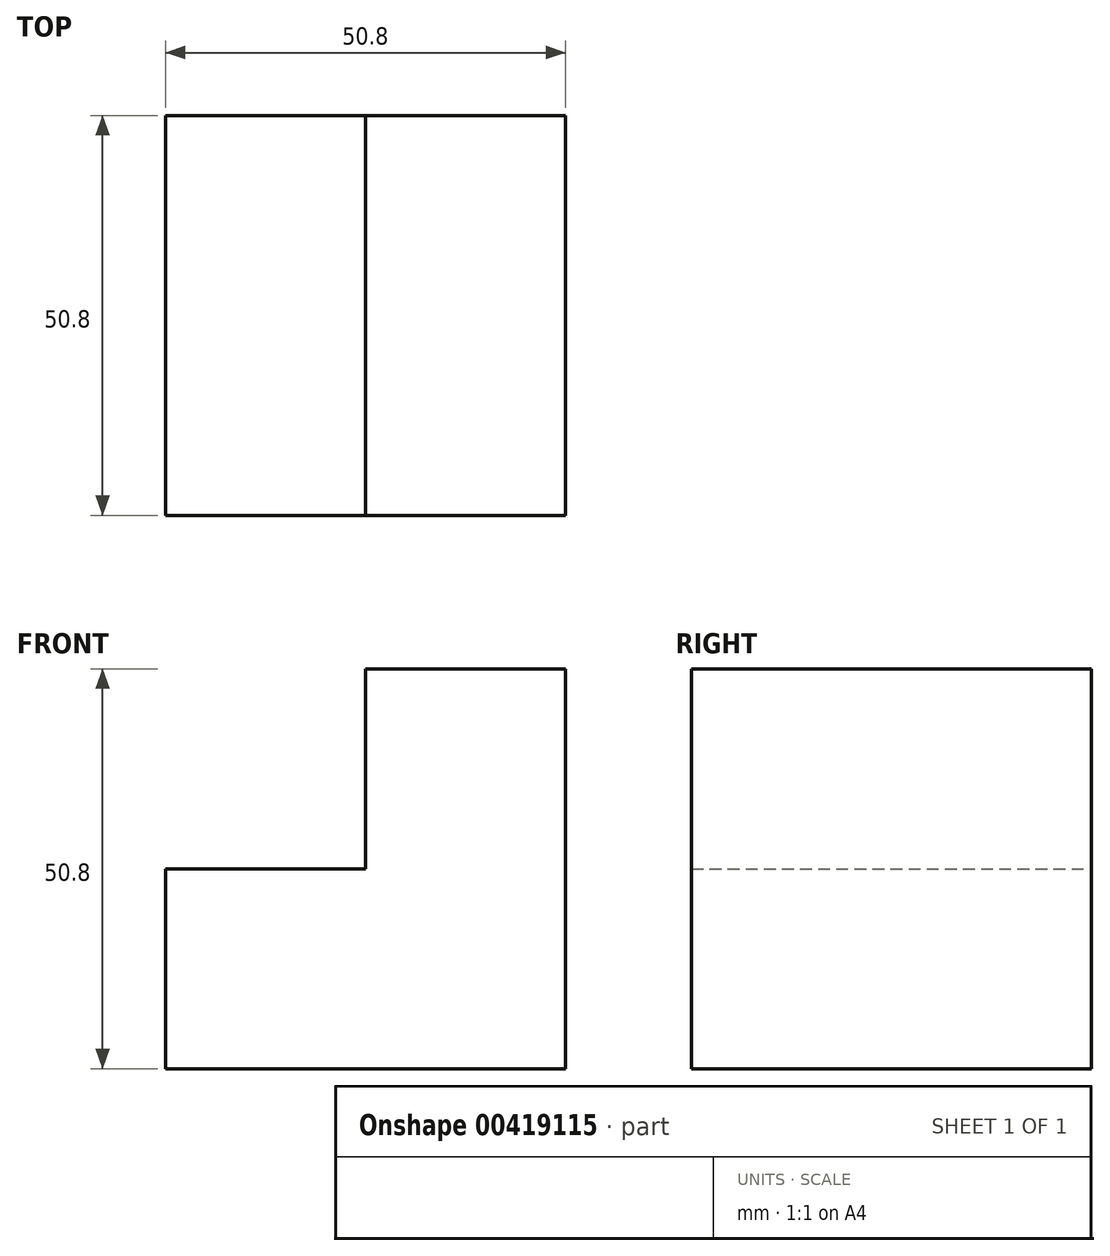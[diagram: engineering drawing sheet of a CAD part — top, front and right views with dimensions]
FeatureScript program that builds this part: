
annotation { "Feature Type Name" : "Feature", "Feature Type Description" : "" }
export const myFeature = defineFeature(function(context is Context, id is Id, definition is map)
    precondition{}
    {
        {
            var Q0;
            Q0=qCreatedBy(makeId("Front.planeOp"),FACE);
            var sketch = newSketch(context, id + "F0", { "sketchPlane" : qUnion([Q0])});
            skLineSegment(sketch, "E0", {"start": v(0, 0) * mm, "end": v(-50.8, 0) * mm});
            skLineSegment(sketch, "E1", {"start": v(0, 0) * mm, "end": v(0, 50.8) * mm});
            skLineSegment(sketch, "E2", {"start": v(-50.8, 0) * mm, "end": v(-50.8, 25.4) * mm});
            skLineSegment(sketch, "E3", {"start": v(-50.8, 25.4) * mm, "end": v(-25.4, 25.4) * mm});
            skLineSegment(sketch, "E4", {"start": v(-25.4, 25.4) * mm, "end": v(-25.4, 50.8) * mm});
            skLineSegment(sketch, "E5", {"start": v(-25.4, 50.8) * mm, "end": v(0, 50.8) * mm});
            skSolve(sketch);
        }
        {
            var Q0;
            Q0 = qSketchRegion(id + "F0", true);
            extrude(context, id + "F1", {"entities" : qUnion([Q0]), "depth" : 50.8 * mm});
        }
    });
